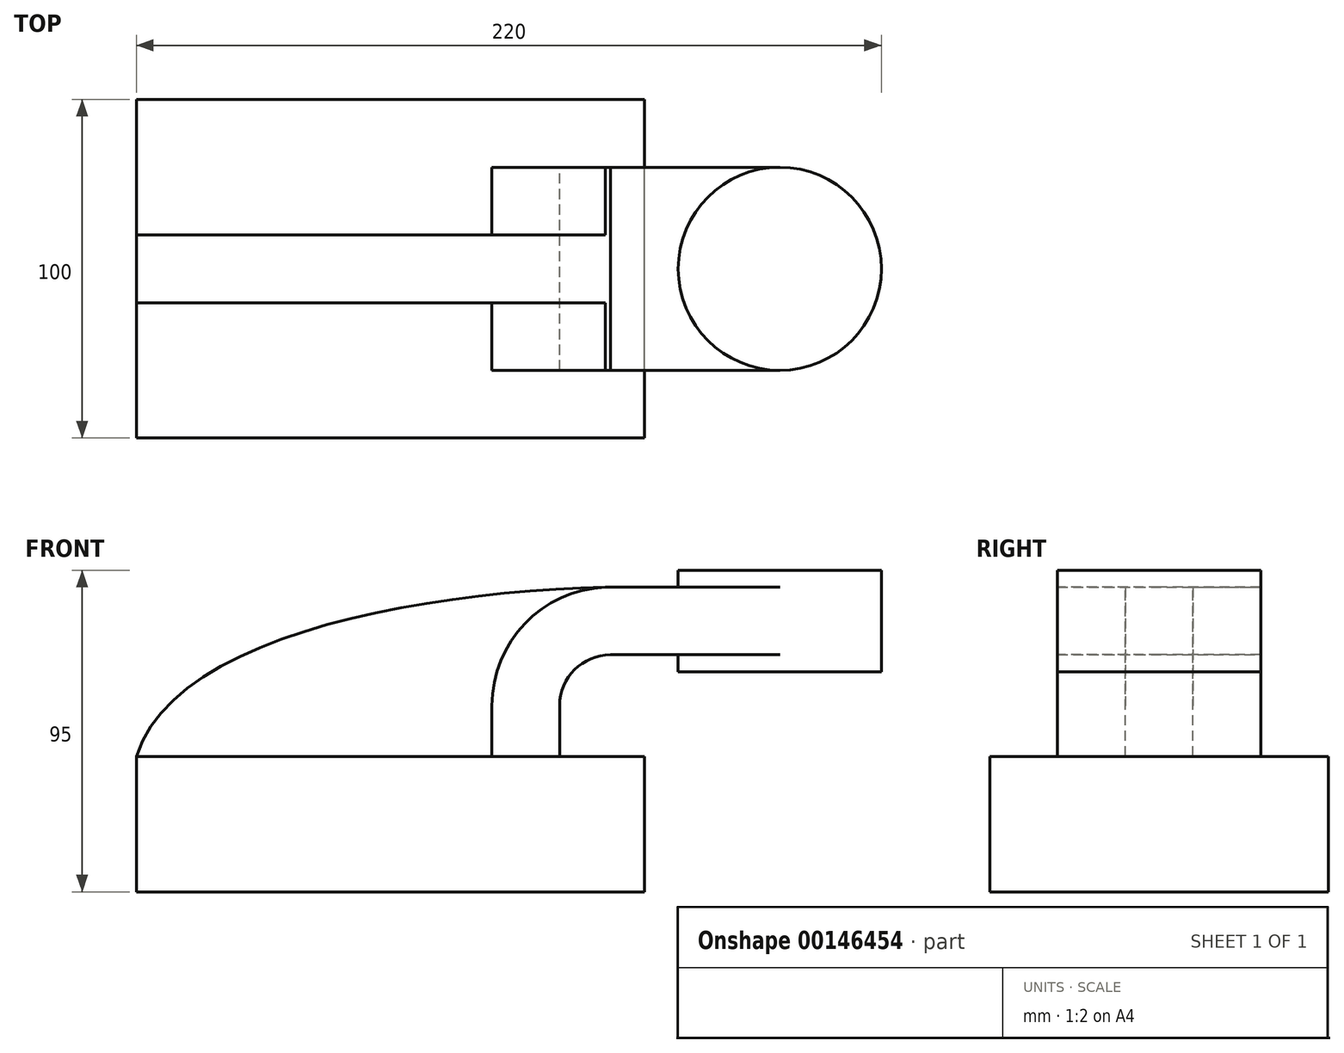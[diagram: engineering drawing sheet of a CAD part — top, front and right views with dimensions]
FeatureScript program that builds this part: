
annotation { "Feature Type Name" : "Feature", "Feature Type Description" : "" }
export const myFeature = defineFeature(function(context is Context, id is Id, definition is map)
    precondition{}
    {
        {
            var Q0;
            Q0=qCreatedBy(makeId("Front.planeOp"),FACE);
            var sketch = newSketch(context, id + "F0", { "sketchPlane" : qUnion([Q0])});
            skLineSegment(sketch, "E0.bottom", {"start": v(-75, 20) * mm, "end": v(75, 20) * mm});
            skLineSegment(sketch, "E0.top", {"start": v(-75, -20) * mm, "end": v(75, -20) * mm});
            skLineSegment(sketch, "E0.left", {"start": v(-75, 20) * mm, "end": v(-75, -20) * mm});
            skLineSegment(sketch, "E0.right", {"start": v(75, 20) * mm, "end": v(75, -20) * mm});
            skPoint(sketch, "E0.middle", {"position": v(0, 0) * mm});
            skLineSegment(sketch, "E1.bottom", {"start": v(145, 45) * mm, "end": v(85, 45) * mm});
            skLineSegment(sketch, "E1.top", {"start": v(145, 75) * mm, "end": v(85, 75) * mm});
            skLineSegment(sketch, "E1.left", {"start": v(145, 45) * mm, "end": v(145, 75) * mm});
            skLineSegment(sketch, "E1.right", {"start": v(85, 45) * mm, "end": v(85, 75) * mm});
            skPoint(sketch, "E1.middle", {"position": v(115, 60) * mm});
            skLineSegment(sketch, "E2", {"start": v(50, 20) * mm, "end": v(50, 35) * mm});
            skArc(sketch, "E3", {"start": v(50, 35) * mm, "mid": v(54.4, 45.6) * mm, "end": v(65, 50) * mm});
            skLineSegment(sketch, "E4", {"start": v(65, 50) * mm, "end": v(115, 50) * mm});
            skLineSegment(sketch, "E5.0", {"start": v(65, 70) * mm, "end": v(115, 70) * mm});
            skArc(sketch, "E5.1", {"start": v(30, 35) * mm, "mid": v(40.25, 59.75) * mm, "end": v(65, 70) * mm});
            skLineSegment(sketch, "E5.2", {"start": v(30, 20) * mm, "end": v(30, 35) * mm});
            skLineSegment(sketch, "E6", {"start": v(115, 45) * mm, "end": v(115, 75) * mm});
            skFitSpline(sketch, "E7", {"points": [v(-75, 20) * mm, v(65, 70) * mm], "startDerivative": vector(33.32, 108.13) * mm, "endDerivative": vector(164.77, 3.28) * mm});
            skSolve(sketch);
        }
        {
            var Q0;
            Q0=makeQuery(id+"F0.imprint","IMPRINT",FACE,{"disambiguationData":[TD([[makeQuery(id+"F0.imprint","IMPRINT",EDGE,{"derivedFrom":sQuery(id+"F0.wireOp",EDGE,"E0.top")}),1.0]])]});
            extrude(context, id + "F1", {"entities" : qUnion([Q0]), "endBound" : BoundingType.SYMMETRIC, "depth" : 100 * mm});
        }
        {
            var Q0;
            {var subQ1=sQuery(id+"F0.wireOp",EDGE,"E2");Q0=makeQuery(id+"F0.imprint","IMPRINT",FACE,{"disambiguationData":[TD([[makeQuery(id+"F0.imprint","IMPRINT",EDGE,{"derivedFrom":subQ1}),1.0]])]});}
            var Q1;
            {var subQ0=sQuery(id+"F0.wireOp",EDGE,"E4");var subQ1=sQuery(id+"F0.wireOp",EDGE,"E1.right");var subQ2=makeQuery(id+"F0.imprint","INTERSECT",VERTEX,{"derivedFrom":[subQ1,subQ0]});Q1=makeQuery(id+"F0.imprint","IMPRINT",FACE,{"disambiguationData":[TD([[makeQuery(id+"F0.imprint","IMPRINT",EDGE,{"disambiguationData":[TD([[subQ2,-1.0]])],"derivedFrom":subQ1}),-1.0]])]});}
            extrude(context, id + "F2", {"entities" : qUnion([Q0, Q1]), "operationType" : NewBodyOperationType.ADD, "endBound" : BoundingType.SYMMETRIC, "depth" : 60 * mm});
        }
        {
            var Q0;
            {var subQ4=sQuery(id+"F0.wireOp",EDGE,"E1.left");Q0=makeQuery(id+"F0.imprint","IMPRINT",FACE,{"disambiguationData":[TD([[makeQuery(id+"F0.imprint","IMPRINT",EDGE,{"derivedFrom":subQ4}),1.0]])]});}
            var Q1;
            Q1=sQuery(id+"F0.wireOp",EDGE,"E6");
            revolve(context, id + "F3", {"operationType" : NewBodyOperationType.ADD, "entities" : qUnion([Q0]), "axis" : qUnion([Q1]), "revolveType" : RevolveType.FULL});
        }
        {
            var Q0;
            {var subQ3=sQuery(id+"F0.wireOp",EDGE,"E5.2");Q0=makeQuery(id+"F0.imprint","IMPRINT",FACE,{"disambiguationData":[TD([[makeQuery(id+"F0.imprint","IMPRINT",EDGE,{"derivedFrom":subQ3}),1.0]])]});}
            extrude(context, id + "F4", {"entities" : qUnion([Q0]), "operationType" : NewBodyOperationType.ADD, "endBound" : BoundingType.SYMMETRIC, "depth" : 20 * mm});
        }
    });
